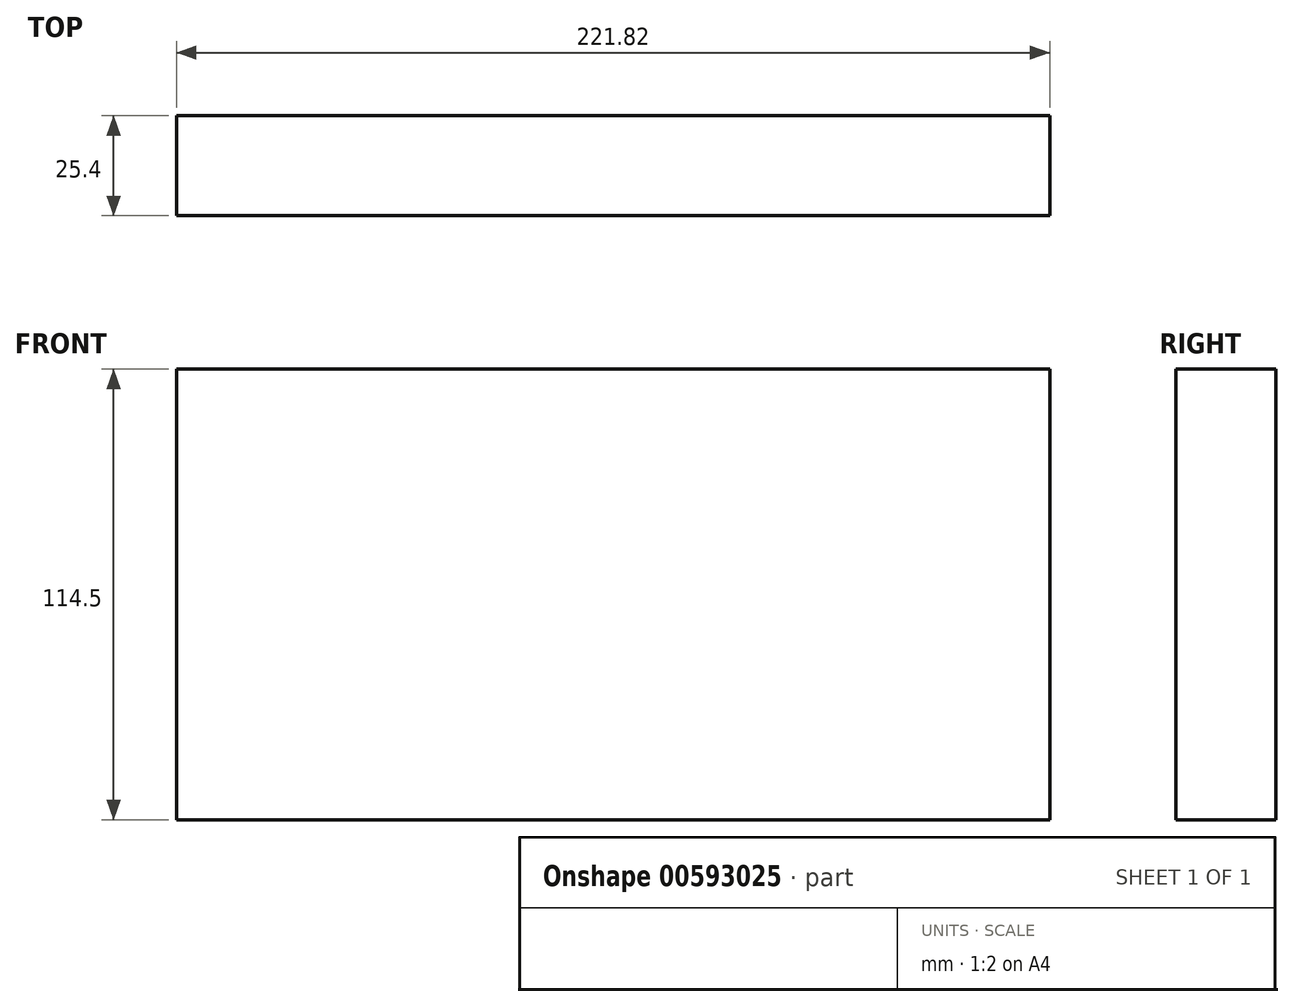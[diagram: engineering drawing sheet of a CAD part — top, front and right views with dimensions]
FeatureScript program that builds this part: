
annotation { "Feature Type Name" : "Feature", "Feature Type Description" : "" }
export const myFeature = defineFeature(function(context is Context, id is Id, definition is map)
    precondition{}
    {
        {
            var Q0;
            Q0=qCreatedBy(makeId("Front.planeOp"),FACE);
            var sketch = newSketch(context, id + "F0", { "sketchPlane" : qUnion([Q0])});
            skLineSegment(sketch, "E0.bottom", {"start": v(110.9, 57.25) * mm, "end": v(-110.9, 57.25) * mm});
            skLineSegment(sketch, "E0.top", {"start": v(110.9, -57.25) * mm, "end": v(-110.9, -57.25) * mm});
            skLineSegment(sketch, "E0.left", {"start": v(110.9, 57.25) * mm, "end": v(110.9, -57.25) * mm});
            skLineSegment(sketch, "E0.right", {"start": v(-110.9, 57.25) * mm, "end": v(-110.9, -57.25) * mm});
            skPoint(sketch, "E0.middle", {"position": v(0, 0) * mm});
            skSolve(sketch);
        }
        {
            var Q0;
            Q0 = qSketchRegion(id + "F0", true);
            extrude(context, id + "F1", {"entities" : qUnion([Q0]), "depth" : 25.4 * mm, "offsetDistance" : 25.4 * mm});
        }
    });
